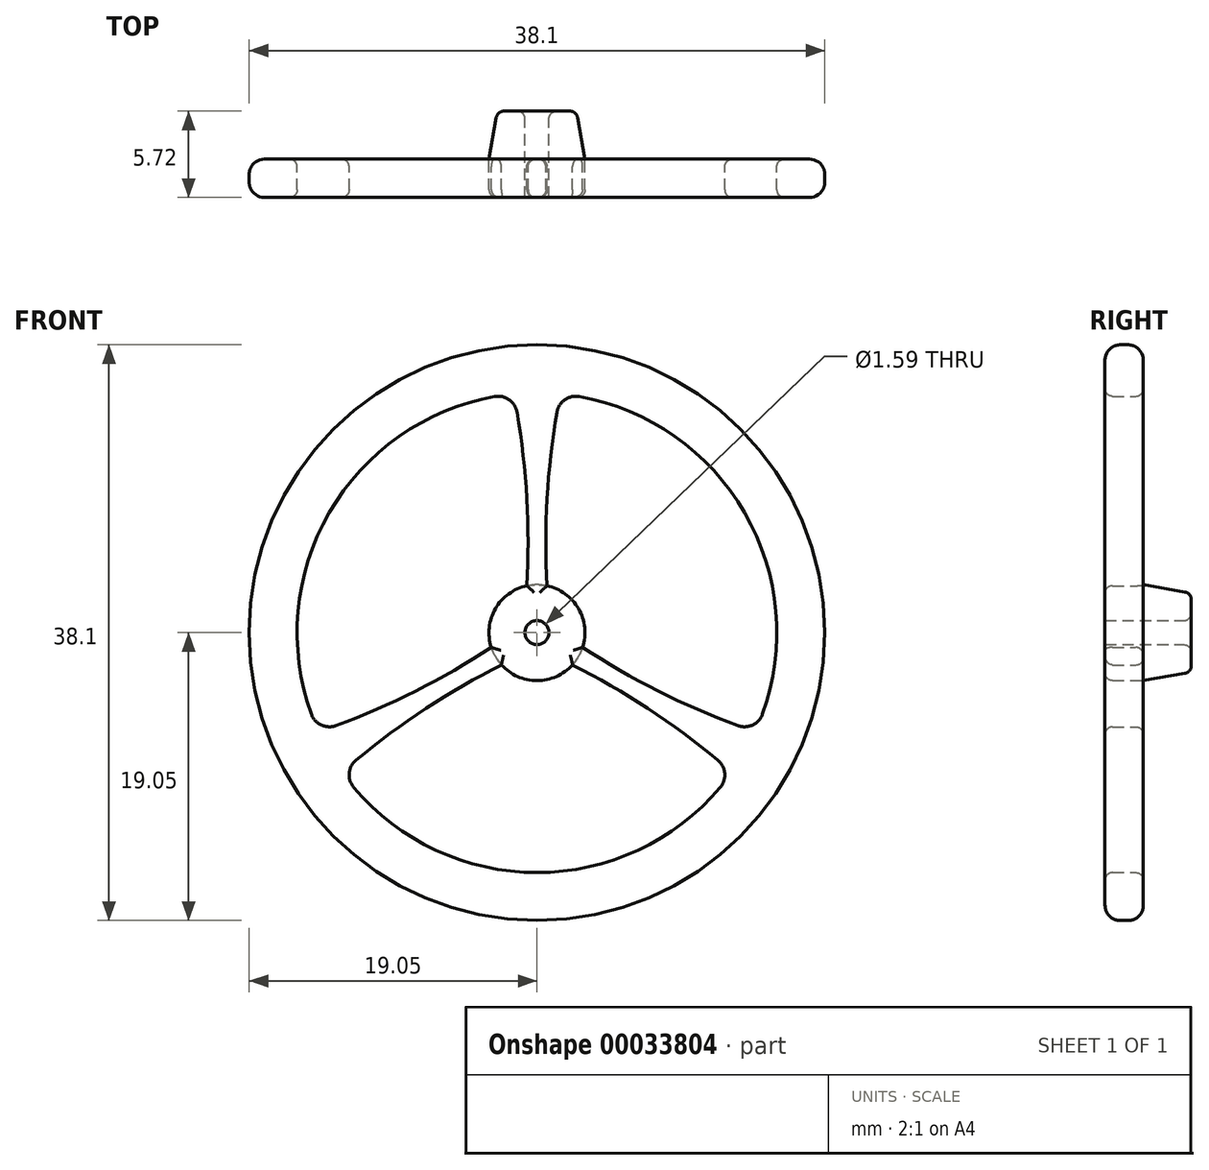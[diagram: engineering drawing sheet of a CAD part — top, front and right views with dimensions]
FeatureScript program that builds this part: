
annotation { "Feature Type Name" : "Feature", "Feature Type Description" : "" }
export const myFeature = defineFeature(function(context is Context, id is Id, definition is map)
    precondition{}
    {
        {
            var Q0;
            Q0=qCreatedBy(makeId("Front.planeOp"),FACE);
            var sketch = newSketch(context, id + "F0", { "sketchPlane" : qUnion([Q0])});
            skArc(sketch, "E0", {"start": v(-2.35, -2.13) * mm, "mid": v(0, -3.17) * mm, "end": v(2.35, -2.13) * mm});
            skArc(sketch, "E1", {"start": v(-2.8, 15.63) * mm, "mid": v(-13.75, 7.94) * mm, "end": v(-14.93, -5.4) * mm});
            skCircle(sketch, "E2", {"center": v(0, 0) * mm, "radius": 19.05 * mm});
            skCircle(sketch, "E3", {"center": v(0, 0) * mm, "radius": 0.8 * mm});
            skArc(sketch, "E4", {"start": v(-0.67, 3.1) * mm, "mid": v(-0.67, 8.87) * mm, "end": v(-1.32, 14.6) * mm});
            skArc(sketch, "E5", {"start": v(-1.32, 14.6) * mm, "mid": v(-1.84, 15.42) * mm, "end": v(-2.8, 15.63) * mm});
            skLineSegment(sketch, "E6", {"start": v(0, 0) * mm, "end": v(0, 19.05) * mm});
            skArc(sketch, "E7.MirrorCS", {"start": v(0.67, 3.1) * mm, "mid": v(0.67, 8.87) * mm, "end": v(1.32, 14.6) * mm});
            skArc(sketch, "E8.MirrorCS", {"start": v(1.32, 14.6) * mm, "mid": v(1.84, 15.42) * mm, "end": v(2.8, 15.63) * mm});
            skArc(sketch, "E9.1.0", {"start": v(-11.98, -8.44) * mm, "mid": v(-12.43, -9.3) * mm, "end": v(-12.13, -10.24) * mm});
            skArc(sketch, "E9.1.1", {"start": v(-2.35, -2.13) * mm, "mid": v(-7.34, -5.01) * mm, "end": v(-11.98, -8.44) * mm});
            skArc(sketch, "E9.1.2", {"start": v(-13.3, -6.15) * mm, "mid": v(-14.27, -6.11) * mm, "end": v(-14.93, -5.4) * mm});
            skArc(sketch, "E9.1.3", {"start": v(-3.02, -0.97) * mm, "mid": v(-8.01, -3.85) * mm, "end": v(-13.3, -6.15) * mm});
            skArc(sketch, "E9.2.0", {"start": v(13.3, -6.15) * mm, "mid": v(14.27, -6.11) * mm, "end": v(14.93, -5.4) * mm});
            skArc(sketch, "E9.2.1", {"start": v(3.02, -0.97) * mm, "mid": v(8.01, -3.85) * mm, "end": v(13.3, -6.15) * mm});
            skArc(sketch, "E9.2.2", {"start": v(11.98, -8.44) * mm, "mid": v(12.43, -9.3) * mm, "end": v(12.13, -10.24) * mm});
            skArc(sketch, "E9.2.3", {"start": v(2.35, -2.13) * mm, "mid": v(7.34, -5.01) * mm, "end": v(11.98, -8.44) * mm});
            skArc(sketch, "E10.trimOffspring", {"start": v(14.93, -5.4) * mm, "mid": v(13.75, 7.94) * mm, "end": v(2.8, 15.63) * mm});
            skArc(sketch, "E11.trimOffspring", {"start": v(-12.13, -10.24) * mm, "mid": v(0, -15.87) * mm, "end": v(12.13, -10.24) * mm});
            skArc(sketch, "E12.trimOffspring", {"start": v(3.02, -0.97) * mm, "mid": v(2.75, 1.59) * mm, "end": v(0.67, 3.1) * mm});
            skArc(sketch, "E13.trimOffspring", {"start": v(-0.67, 3.1) * mm, "mid": v(-2.75, 1.59) * mm, "end": v(-3.02, -0.97) * mm});
            skSolve(sketch);
        }
        {
            var Q0;
            Q0 = qSketchRegion(id + "F0", true);
            extrude(context, id + "F1", {"entities" : qUnion([Q0]), "depth" : 2.54 * mm});
        }
        {
            var Q0;
            Q0=qCreatedBy(makeId("Front.planeOp"),FACE);
            var sketch = newSketch(context, id + "F2", { "sketchPlane" : qUnion([Q0])});
            skCircle(sketch, "E14", {"center": v(0, 0) * mm, "radius": 3.18 * mm});
            skSolve(sketch);
        }
        {
            var Q0;
            Q0 = qSketchRegion(id + "F2", true);
            extrude(context, id + "F3", {"entities" : qUnion([Q0]), "operationType" : NewBodyOperationType.ADD, "oppositeDirection" : true, "depth" : 3.17 * mm, "hasDraft" : true, "draftAngle" : 10 * degree, "draftPullDirection" : true});
        }
        {
            var Q0;
            Q0=makeQuery(id+"F1.opExtrude","CAP_FACE",FACE,{"disambiguationData":[OSD([sQuery(id+"F0.wireOp",EDGE,"E0"),sQuery(id+"F0.wireOp",EDGE,"E1"),sQuery(id+"F0.wireOp",EDGE,"E2"),sQuery(id+"F0.wireOp",EDGE,"E3"),sQuery(id+"F0.wireOp",EDGE,"E4"),sQuery(id+"F0.wireOp",EDGE,"E5"),sQuery(id+"F0.wireOp",EDGE,"E7.MirrorCS"),sQuery(id+"F0.wireOp",EDGE,"E8.MirrorCS"),sQuery(id+"F0.wireOp",EDGE,"E9.1.0"),sQuery(id+"F0.wireOp",EDGE,"E9.1.1"),sQuery(id+"F0.wireOp",EDGE,"E9.1.2"),sQuery(id+"F0.wireOp",EDGE,"E9.1.3"),sQuery(id+"F0.wireOp",EDGE,"E9.2.0"),sQuery(id+"F0.wireOp",EDGE,"E9.2.1"),sQuery(id+"F0.wireOp",EDGE,"E9.2.2"),sQuery(id+"F0.wireOp",EDGE,"E9.2.3"),sQuery(id+"F0.wireOp",EDGE,"E10.trimOffspring"),sQuery(id+"F0.wireOp",EDGE,"E11.trimOffspring"),sQuery(id+"F0.wireOp",EDGE,"E12.trimOffspring"),sQuery(id+"F0.wireOp",EDGE,"E13.trimOffspring")])],"isStart":false});
            var sketch = newSketch(context, id + "F4", { "sketchPlane" : qUnion([Q0])});
            skCircle(sketch, "E15.0", {"center": v(0, 0) * mm, "radius": 0.8 * mm});
            skSolve(sketch);
        }
        {
            var Q0;
            Q0 = qSketchRegion(id + "F4", true);
            extrude(context, id + "F5", {"entities" : qUnion([Q0]), "operationType" : NewBodyOperationType.REMOVE, "endBound" : BoundingType.THROUGH_ALL, "oppositeDirection" : true, "depth" : 25.4 * mm});
        }
        {
            var Q0;
            Q0=makeQuery(id+"F3.opExtrude","CAP_FACE",FACE,{"disambiguationData":[OSD([sQuery(id+"F2.wireOp",EDGE,"E14")])],"isStart":false});
            fillet(context, id + "F6", {"entities" : qUnion([Q0]), "radius" : 0.5 * mm, "tangentPropagation" : true, "allowEdgeOverflow" : false});
        }
        {
            var Q0;
            Q0=makeQuery(id+"F1.opExtrude","CAP_EDGE",EDGE,{"disambiguationData":[OSD([sQuery(id+"F0.wireOp",EDGE,"E10.trimOffspring")])],"isStart":true});
            var Q1;
            Q1=makeQuery(id+"F1.opExtrude","CAP_EDGE",EDGE,{"disambiguationData":[OSD([sQuery(id+"F0.wireOp",EDGE,"E9.2.0")])],"isStart":true});
            var Q2;
            Q2=makeQuery(id+"F1.opExtrude","CAP_EDGE",EDGE,{"disambiguationData":[OSD([sQuery(id+"F0.wireOp",EDGE,"E9.2.1")])],"isStart":true});
            var Q3;
            Q3=makeQuery(id+"F1.opExtrude","CAP_EDGE",EDGE,{"disambiguationData":[OSD([sQuery(id+"F0.wireOp",EDGE,"E7.MirrorCS")])],"isStart":true});
            var Q4;
            Q4=makeQuery(id+"F1.opExtrude","CAP_EDGE",EDGE,{"disambiguationData":[OSD([sQuery(id+"F0.wireOp",EDGE,"E8.MirrorCS")])],"isStart":true});
            var Q5;
            Q5=makeQuery(id+"F1.opExtrude","CAP_EDGE",EDGE,{"disambiguationData":[OSD([sQuery(id+"F0.wireOp",EDGE,"E5")])],"isStart":true});
            var Q6;
            Q6=makeQuery(id+"F1.opExtrude","CAP_EDGE",EDGE,{"disambiguationData":[OSD([sQuery(id+"F0.wireOp",EDGE,"E4")])],"isStart":true});
            var Q7;
            Q7=makeQuery(id+"F1.opExtrude","CAP_EDGE",EDGE,{"disambiguationData":[OSD([sQuery(id+"F0.wireOp",EDGE,"E1")])],"isStart":true});
            var Q8;
            Q8=makeQuery(id+"F1.opExtrude","CAP_EDGE",EDGE,{"disambiguationData":[OSD([sQuery(id+"F0.wireOp",EDGE,"E9.1.2")])],"isStart":true});
            var Q9;
            Q9=makeQuery(id+"F1.opExtrude","CAP_EDGE",EDGE,{"disambiguationData":[OSD([sQuery(id+"F0.wireOp",EDGE,"E9.1.3")])],"isStart":true});
            var Q10;
            Q10=makeQuery(id+"F1.opExtrude","CAP_EDGE",EDGE,{"disambiguationData":[OSD([sQuery(id+"F0.wireOp",EDGE,"E9.1.1")])],"isStart":true});
            var Q11;
            Q11=makeQuery(id+"F1.opExtrude","CAP_EDGE",EDGE,{"disambiguationData":[OSD([sQuery(id+"F0.wireOp",EDGE,"E9.1.0")])],"isStart":true});
            var Q12;
            Q12=makeQuery(id+"F1.opExtrude","CAP_EDGE",EDGE,{"disambiguationData":[OSD([sQuery(id+"F0.wireOp",EDGE,"E11.trimOffspring")])],"isStart":true});
            var Q13;
            Q13=makeQuery(id+"F1.opExtrude","CAP_EDGE",EDGE,{"disambiguationData":[OSD([sQuery(id+"F0.wireOp",EDGE,"E9.2.2")])],"isStart":true});
            var Q14;
            Q14=makeQuery(id+"F1.opExtrude","CAP_EDGE",EDGE,{"disambiguationData":[OSD([sQuery(id+"F0.wireOp",EDGE,"E9.2.3")])],"isStart":true});
            fillet(context, id + "F7", {"entities" : qUnion([Q0, Q1, Q2, Q3, Q4, Q5, Q6, Q7, Q8, Q9, Q10, Q11, Q12, Q13, Q14]), "radius" : 0.5 * mm, "tangentPropagation" : true, "allowEdgeOverflow" : false});
        }
        {
            var Q0;
            Q0=makeQuery(id+"F1.opExtrude","CAP_EDGE",EDGE,{"disambiguationData":[OSD([sQuery(id+"F0.wireOp",EDGE,"E4")])],"isStart":false});
            var Q1;
            Q1=makeQuery(id+"F1.opExtrude","CAP_EDGE",EDGE,{"disambiguationData":[OSD([sQuery(id+"F0.wireOp",EDGE,"E5")])],"isStart":false});
            var Q2;
            Q2=makeQuery(id+"F1.opExtrude","CAP_EDGE",EDGE,{"disambiguationData":[OSD([sQuery(id+"F0.wireOp",EDGE,"E1")])],"isStart":false});
            var Q3;
            Q3=makeQuery(id+"F1.opExtrude","CAP_EDGE",EDGE,{"disambiguationData":[OSD([sQuery(id+"F0.wireOp",EDGE,"E9.1.2")])],"isStart":false});
            var Q4;
            Q4=makeQuery(id+"F1.opExtrude","CAP_EDGE",EDGE,{"disambiguationData":[OSD([sQuery(id+"F0.wireOp",EDGE,"E9.1.3")])],"isStart":false});
            var Q5;
            Q5=makeQuery(id+"F1.opExtrude","CAP_EDGE",EDGE,{"disambiguationData":[OSD([sQuery(id+"F0.wireOp",EDGE,"E9.1.1")])],"isStart":false});
            var Q6;
            Q6=makeQuery(id+"F1.opExtrude","CAP_EDGE",EDGE,{"disambiguationData":[OSD([sQuery(id+"F0.wireOp",EDGE,"E9.1.0")])],"isStart":false});
            var Q7;
            Q7=makeQuery(id+"F1.opExtrude","CAP_EDGE",EDGE,{"disambiguationData":[OSD([sQuery(id+"F0.wireOp",EDGE,"E11.trimOffspring")])],"isStart":false});
            var Q8;
            Q8=makeQuery(id+"F1.opExtrude","CAP_EDGE",EDGE,{"disambiguationData":[OSD([sQuery(id+"F0.wireOp",EDGE,"E9.2.2")])],"isStart":false});
            var Q9;
            Q9=makeQuery(id+"F1.opExtrude","CAP_EDGE",EDGE,{"disambiguationData":[OSD([sQuery(id+"F0.wireOp",EDGE,"E9.2.3")])],"isStart":false});
            var Q10;
            Q10=makeQuery(id+"F1.opExtrude","CAP_EDGE",EDGE,{"disambiguationData":[OSD([sQuery(id+"F0.wireOp",EDGE,"E9.2.1")])],"isStart":false});
            var Q11;
            Q11=makeQuery(id+"F1.opExtrude","CAP_EDGE",EDGE,{"disambiguationData":[OSD([sQuery(id+"F0.wireOp",EDGE,"E9.2.0")])],"isStart":false});
            var Q12;
            Q12=makeQuery(id+"F1.opExtrude","CAP_EDGE",EDGE,{"disambiguationData":[OSD([sQuery(id+"F0.wireOp",EDGE,"E10.trimOffspring")])],"isStart":false});
            var Q13;
            Q13=makeQuery(id+"F1.opExtrude","CAP_EDGE",EDGE,{"disambiguationData":[OSD([sQuery(id+"F0.wireOp",EDGE,"E8.MirrorCS")])],"isStart":false});
            var Q14;
            Q14=makeQuery(id+"F1.opExtrude","CAP_EDGE",EDGE,{"disambiguationData":[OSD([sQuery(id+"F0.wireOp",EDGE,"E7.MirrorCS")])],"isStart":false});
            fillet(context, id + "F8", {"entities" : qUnion([Q0, Q1, Q2, Q3, Q4, Q5, Q6, Q7, Q8, Q9, Q10, Q11, Q12, Q13, Q14]), "radius" : 0.5 * mm, "tangentPropagation" : true, "allowEdgeOverflow" : false});
        }
        {
            var Q0;
            Q0=makeQuery(id+"F1.opExtrude","CAP_EDGE",EDGE,{"disambiguationData":[OSD([sQuery(id+"F0.wireOp",EDGE,"E12.trimOffspring")])],"isStart":false});
            var Q1;
            Q1=makeQuery(id+"F1.opExtrude","CAP_EDGE",EDGE,{"disambiguationData":[OSD([sQuery(id+"F0.wireOp",EDGE,"E0")])],"isStart":false});
            var Q2;
            Q2=makeQuery(id+"F1.opExtrude","CAP_EDGE",EDGE,{"disambiguationData":[OSD([sQuery(id+"F0.wireOp",EDGE,"E13.trimOffspring")])],"isStart":false});
            fillet(context, id + "F9", {"entities" : qUnion([Q0, Q1, Q2]), "radius" : 0.5 * mm, "tangentPropagation" : true, "allowEdgeOverflow" : false});
        }
        {
            var Q0;
            Q0=makeQuery(id+"F1.opExtrude","SWEPT_FACE",FACE,{"disambiguationData":[OSD([sQuery(id+"F0.wireOp",EDGE,"E2")])]});
            fillet(context, id + "F10", {"entities" : qUnion([Q0]), "radius" : 1.02 * mm, "tangentPropagation" : true, "allowEdgeOverflow" : false});
        }
    });
